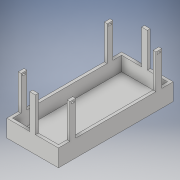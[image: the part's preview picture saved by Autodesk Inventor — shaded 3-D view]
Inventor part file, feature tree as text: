
AUTODESK INVENTOR PART (.ipt)
format: ipt  version: 2017 (Build 210142000, 142)  size: 233,984 bytes
history: native  units: in
note: dims shown in document units (in); Inventor stores cm internally (conversion verified against a paired STEP export)
features: extrude x4, sketch x4
ambient origin geometry x8: Origin, YZ Plane, XZ Plane, XY Plane, X Axis, Y Axis, Z Axis, Center Point
bodies: Solid1 (feature_tree)
feature tree (8):
  extrude  "Extrusion1"  Depth=0.125in
  extrude  "Extrusion2"  Depth=0.125in
  extrude  "Extrusion3"  Depth=0.125in
  extrude  "Extrusion4"  Depth=0.25in
  sketch  "Sketch1"  dims[d2=0.125in d3=0.125in]
  sketch  "Sketch2"  dims[d7=0.25in d8=0.125in]
  sketch  "Sketch3"  dims[d9=0.125in d10=0.125in]
  sketch  "Sketch5"  dims[d11=0.125in d12=0.25in d13=0.25in d14=0.125in d15=0.125in d16=0.25in d17=0.25in d18=0.125in d19=0.75in d20=0.0in d21=0.125in d22=0.0in d23=5.0in d24=2.25in d42=1.5in d43=0.0in d45=0.25in d46=0.125in d49=0.125in d50=0.25in d51=0.25in d52=0.25in d53=0.25in d54=0.125in d55=0.0in d56=1.125in d57=0.25in d58=0.125in d59=0.0in d60=1.125in d61=0.25in d62=0.125in d63=0.0625in d64=0.0625in d66=0.0625in d67=0.125in d68=0.0625in d69=999.0in d70=0.0in d71=0.5in d72=0.5in d73=0.5in d74=0.5in d88=0.0625in d89=0.0625in]
